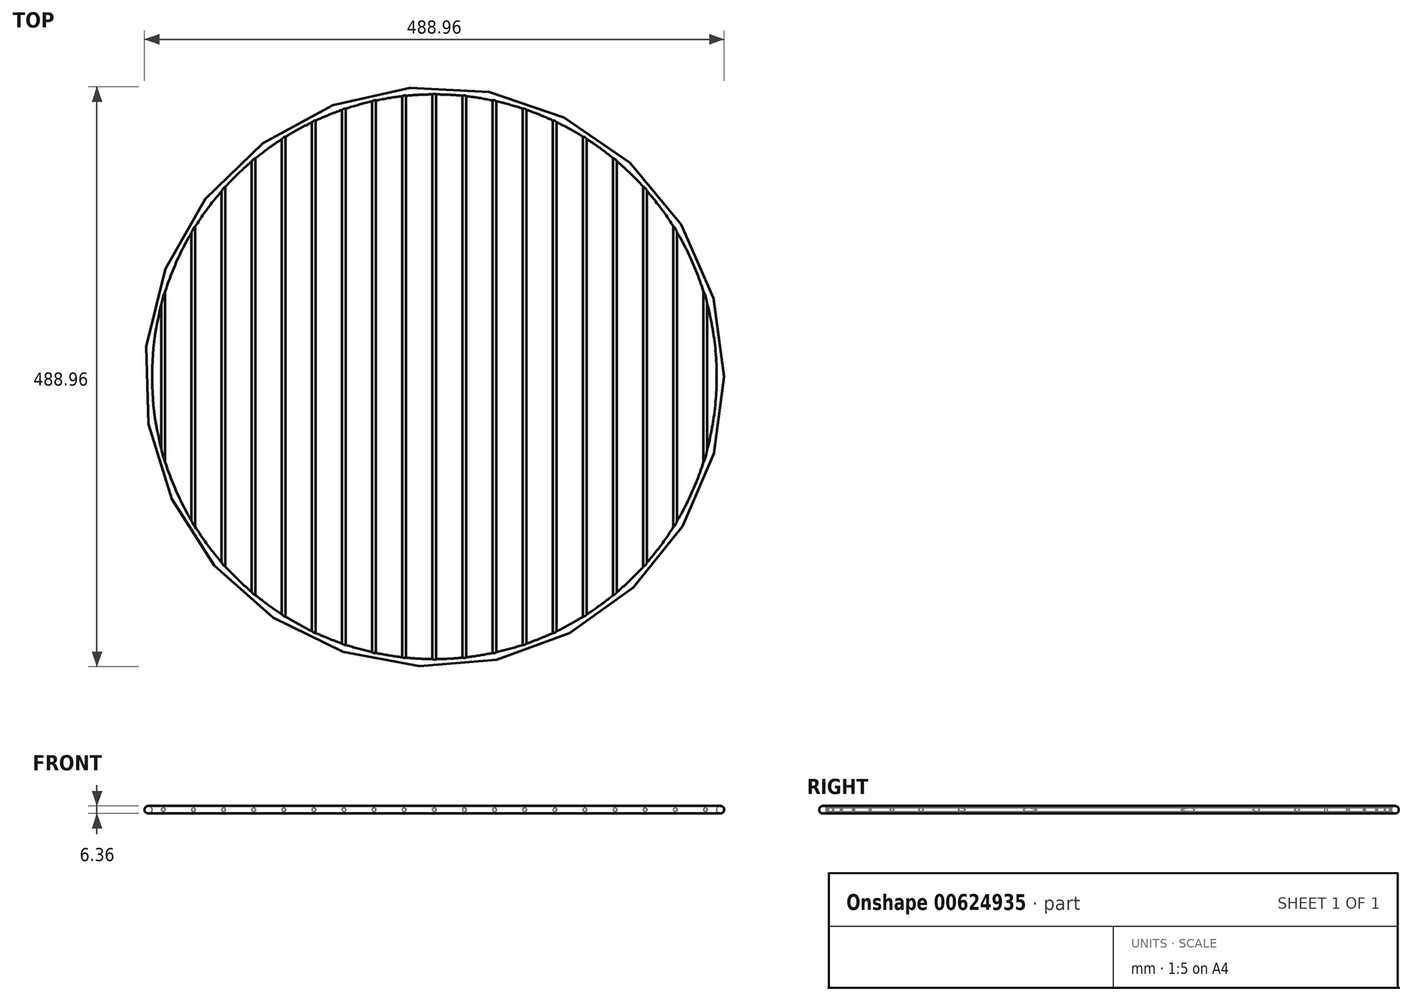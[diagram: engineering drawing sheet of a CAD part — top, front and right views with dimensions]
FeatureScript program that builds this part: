
annotation { "Feature Type Name" : "Feature", "Feature Type Description" : "" }
export const myFeature = defineFeature(function(context is Context, id is Id, definition is map)
    precondition{}
    {
        {
            var Q0;
            Q0=qCreatedBy(makeId("Front.planeOp"),FACE);
            var sketch = newSketch(context, id + "F0", { "sketchPlane" : qUnion([Q0])});
            skCircle(sketch, "E0", {"center": v(241.3, 0) * mm, "radius": 3.18 * mm});
            skLineSegment(sketch, "E1", {"start": v(0, 0) * mm, "end": v(0, 32.12) * mm, "construction": true});
            skSolve(sketch);
        }
        {
            var Q0;
            Q0=qCreatedBy(makeId("Front.planeOp"),FACE);
            var sketch = newSketch(context, id + "F1", { "sketchPlane" : qUnion([Q0])});
            skCircle(sketch, "E2", {"center": v(0, 0) * mm, "radius": 1.59 * mm});
            skCircle(sketch, "E3.1.0.0", {"center": v(25.4, 0) * mm, "radius": 1.59 * mm});
            skCircle(sketch, "E3.2.0.0", {"center": v(50.8, 0) * mm, "radius": 1.59 * mm});
            skCircle(sketch, "E3.3.0.0", {"center": v(76.2, 0) * mm, "radius": 1.59 * mm});
            skCircle(sketch, "E3.4.0.0", {"center": v(101.6, 0) * mm, "radius": 1.59 * mm});
            skCircle(sketch, "E3.5.0.0", {"center": v(127, 0) * mm, "radius": 1.59 * mm});
            skCircle(sketch, "E3.6.0.0", {"center": v(152.4, 0) * mm, "radius": 1.59 * mm});
            skCircle(sketch, "E3.7.0.0", {"center": v(177.8, 0) * mm, "radius": 1.59 * mm});
            skCircle(sketch, "E3.8.0.0", {"center": v(203.2, 0) * mm, "radius": 1.59 * mm});
            skCircle(sketch, "E3.9.0.0", {"center": v(228.6, 0) * mm, "radius": 1.59 * mm});
            skLineSegment(sketch, "E3.direction1", {"start": v(0, 0) * mm, "end": v(25.4, 0) * mm, "construction": true});
            skCircle(sketch, "E4.1.0.0", {"center": v(-25.4, 0) * mm, "radius": 1.59 * mm});
            skCircle(sketch, "E4.2.0.0", {"center": v(-50.8, 0) * mm, "radius": 1.59 * mm});
            skCircle(sketch, "E4.3.0.0", {"center": v(-76.2, 0) * mm, "radius": 1.59 * mm});
            skCircle(sketch, "E4.4.0.0", {"center": v(-101.6, 0) * mm, "radius": 1.59 * mm});
            skCircle(sketch, "E4.5.0.0", {"center": v(-127, 0) * mm, "radius": 1.59 * mm});
            skCircle(sketch, "E4.6.0.0", {"center": v(-152.4, 0) * mm, "radius": 1.59 * mm});
            skCircle(sketch, "E4.7.0.0", {"center": v(-177.8, 0) * mm, "radius": 1.59 * mm});
            skCircle(sketch, "E4.8.0.0", {"center": v(-203.2, 0) * mm, "radius": 1.59 * mm});
            skCircle(sketch, "E4.9.0.0", {"center": v(-228.6, 0) * mm, "radius": 1.59 * mm});
            skLineSegment(sketch, "E4.direction1", {"start": v(0, 0) * mm, "end": v(-25.4, 0) * mm, "construction": true});
            skSolve(sketch);
        }
        {
            var Q0;
            Q0=makeQuery(id+"F0.imprint","IMPRINT",FACE,{"disambiguationData":[TD([[makeQuery(id+"F0.imprint","IMPRINT",EDGE,{"derivedFrom":sQuery(id+"F0.wireOp",EDGE,"E0")}),1.0]])]});
            var Q1;
            Q1=sQuery(id+"F0.wireOp",EDGE,"E1");
            revolve(context, id + "F2", {"entities" : qUnion([Q0]), "axis" : qUnion([Q1]), "revolveType" : RevolveType.FULL});
        }
        {
            var Q0;
            Q0=qSketchRegion(id+"F1",true);
            extrude(context, id + "F3", {"entities" : qUnion([Q0]), "operationType" : NewBodyOperationType.ADD, "endBound" : BoundingType.UP_TO_NEXT, "depth" : 25.4 * mm, "hasSecondDirection" : true, "secondDirectionBound" : SecondDirectionBoundingType.UP_TO_NEXT, "secondDirectionOppositeDirection" : true, "secondDirectionDepth" : 25.4 * mm});
        }
    });
